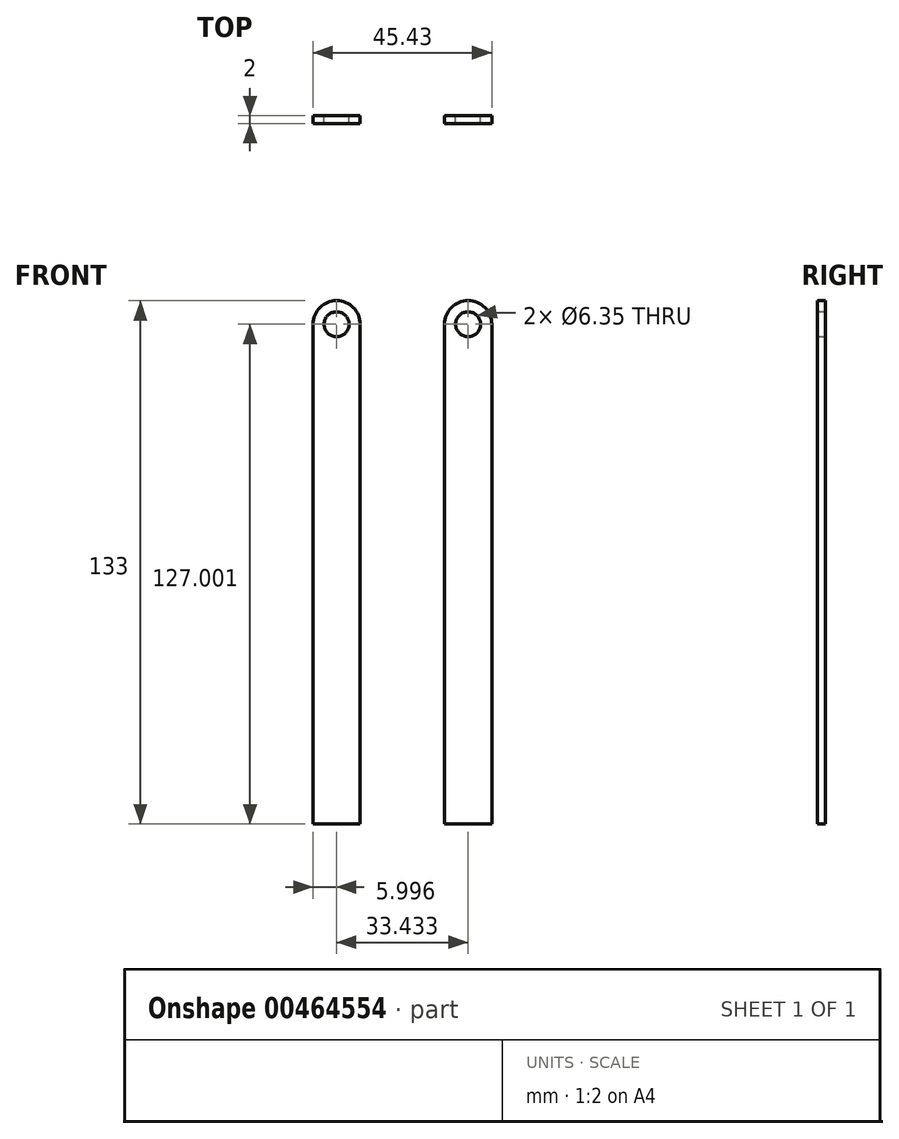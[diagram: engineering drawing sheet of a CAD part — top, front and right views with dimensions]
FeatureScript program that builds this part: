
annotation { "Feature Type Name" : "Feature", "Feature Type Description" : "" }
export const myFeature = defineFeature(function(context is Context, id is Id, definition is map)
    precondition{}
    {
        {
            var Q0;
            Q0=qCreatedBy(makeId("Front.planeOp"),FACE);
            var sketch = newSketch(context, id + "F0", { "sketchPlane" : qUnion([Q0])});
            skLineSegment(sketch, "E0", {"start": v(-142.65, 124.02) * mm, "end": v(-142.65, -2.98) * mm, "construction": true});
            skLineSegment(sketch, "E1", {"start": v(-111.94, 120.41) * mm, "end": v(-111.94, -6.59) * mm});
            skLineSegment(sketch, "E2", {"start": v(-111.94, -6.59) * mm, "end": v(-123.94, -6.59) * mm});
            skLineSegment(sketch, "E3", {"start": v(-123.94, -6.59) * mm, "end": v(-123.94, 120.41) * mm});
            skArc(sketch, "E4", {"start": v(-111.94, 120.41) * mm, "mid": v(-117.94, 126.41) * mm, "end": v(-123.94, 120.41) * mm});
            skLineSegment(sketch, "E5", {"start": v(-90.51, 120.41) * mm, "end": v(-90.51, -6.59) * mm});
            skLineSegment(sketch, "E6", {"start": v(-90.51, -6.59) * mm, "end": v(-78.51, -6.59) * mm});
            skLineSegment(sketch, "E7", {"start": v(-78.51, -6.59) * mm, "end": v(-78.51, 120.41) * mm});
            skArc(sketch, "E8", {"start": v(-78.51, 120.41) * mm, "mid": v(-84.51, 126.41) * mm, "end": v(-90.51, 120.41) * mm});
            skCircle(sketch, "E9", {"center": v(-84.51, 120.41) * mm, "radius": 2.22 * mm});
            skCircle(sketch, "E10", {"center": v(-117.94, 120.41) * mm, "radius": 2.22 * mm});
            skSolve(sketch);
        }
        {
            var Q0;
            Q0=makeQuery(id+"F0.imprint","IMPRINT",FACE,{"disambiguationData":[TD([[makeQuery(id+"F0.imprint","IMPRINT",EDGE,{"derivedFrom":sQuery(id+"F0.wireOp",EDGE,"E1")}),-1.0]])]});
            var Q1;
            Q1=makeQuery(id+"F0.imprint","IMPRINT",FACE,{"disambiguationData":[TD([[makeQuery(id+"F0.imprint","IMPRINT",EDGE,{"derivedFrom":sQuery(id+"F0.wireOp",EDGE,"E5")}),1.0]])]});
            extrude(context, id + "F1", {"entities" : qUnion([Q0, Q1]), "depth" : 2 * mm});
        }
        {
            var Q0;
            Q0=sQuery(id+"F0.wireOp",VERTEX,"E4.center");
            var Q1;
            Q1=sQuery(id+"F0.wireOp",VERTEX,"E9.center");
            var Q2;
            Q2=makeQuery(id+"F1.opExtrude","SWEPT_BODY",BODY,{"disambiguationData":[OSD([sQuery(id+"F0.wireOp",EDGE,"E1"),sQuery(id+"F0.wireOp",EDGE,"E2"),sQuery(id+"F0.wireOp",EDGE,"E3"),sQuery(id+"F0.wireOp",EDGE,"E4"),sQuery(id+"F0.wireOp",EDGE,"E10")])]});
            var Q3;
            Q3=makeQuery(id+"F1.opExtrude","SWEPT_BODY",BODY,{"disambiguationData":[OSD([sQuery(id+"F0.wireOp",EDGE,"E5"),sQuery(id+"F0.wireOp",EDGE,"E6"),sQuery(id+"F0.wireOp",EDGE,"E7"),sQuery(id+"F0.wireOp",EDGE,"E8"),sQuery(id+"F0.wireOp",EDGE,"E9")])]});
            hole(context, id + "F2", {"style" : HoleStyle.SIMPLE, "endStyle" : HoleEndStyle.THROUGH, "oppositeDirection" : true, "holeDiameter" : 6.35 * mm, "isTappedThrough" : true, "tappedDepth" : 12.7 * mm, "tapClearance" : 3, "locations" : qUnion([Q0, Q1]), "scope" : qUnion([Q2, Q3])});
        }
    });
